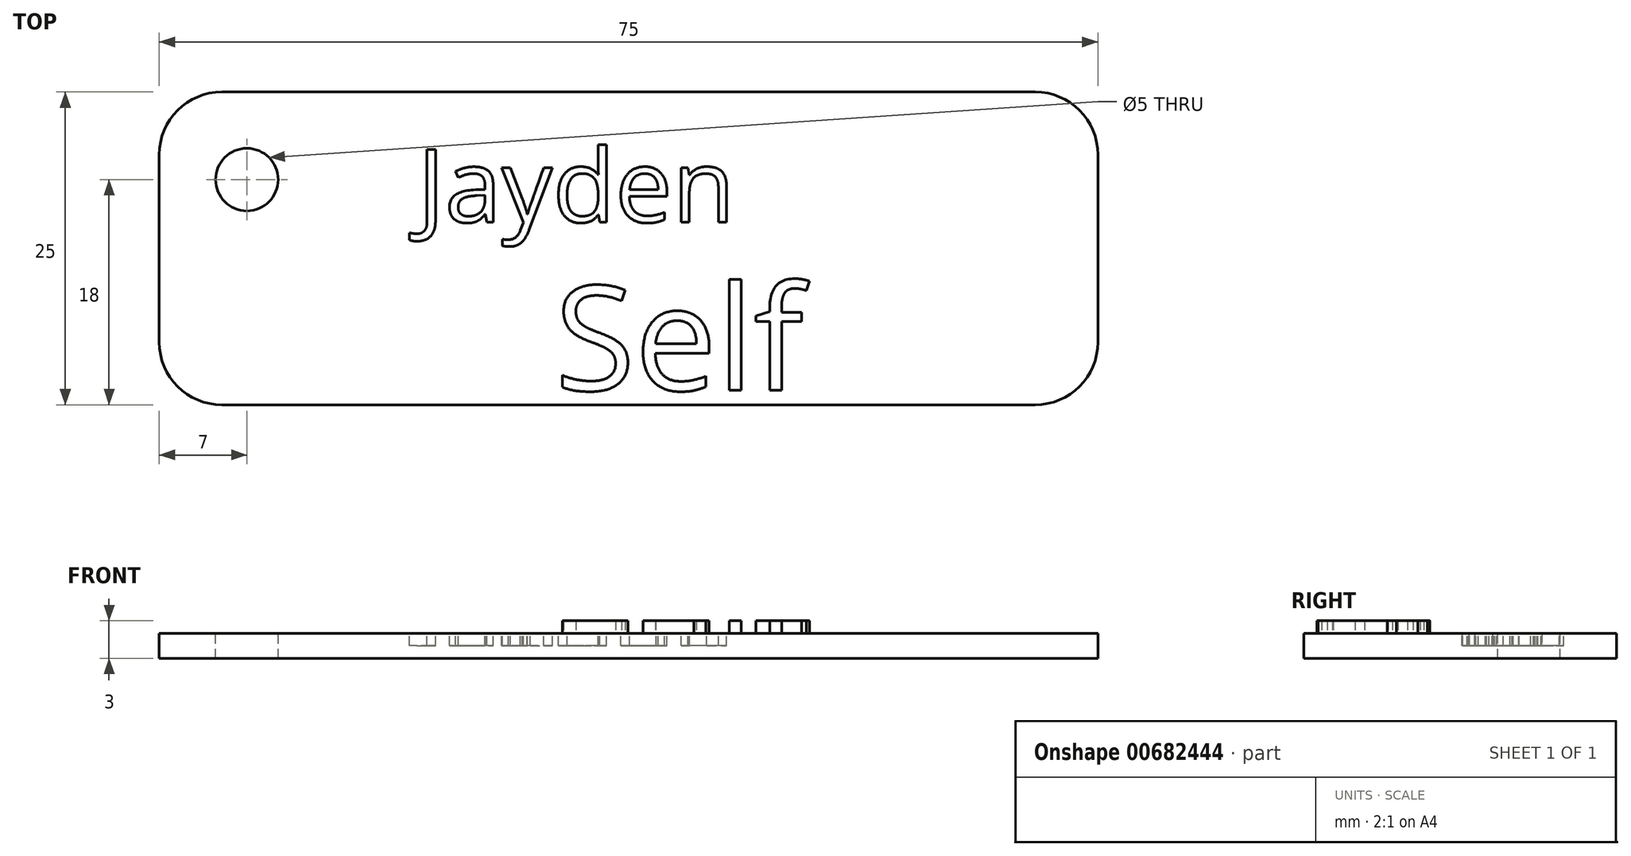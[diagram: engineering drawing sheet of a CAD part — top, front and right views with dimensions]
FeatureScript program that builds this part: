
annotation { "Feature Type Name" : "Feature", "Feature Type Description" : "" }
export const myFeature = defineFeature(function(context is Context, id is Id, definition is map)
    precondition{}
    {
        {
            var Q0;
            Q0=qCreatedBy(makeId("Top.planeOp"),FACE);
            var sketch = newSketch(context, id + "F0", { "sketchPlane" : qUnion([Q0])});
            skLineSegment(sketch, "E0.bottom", {"start": v(-32.5, 12.5) * mm, "end": v(32.5, 12.5) * mm});
            skLineSegment(sketch, "E0.top", {"start": v(-32.5, -12.5) * mm, "end": v(32.5, -12.5) * mm});
            skLineSegment(sketch, "E0.left", {"start": v(-37.5, 7.5) * mm, "end": v(-37.5, -7.5) * mm});
            skLineSegment(sketch, "E0.right", {"start": v(37.5, 7.5) * mm, "end": v(37.5, -7.5) * mm});
            skPoint(sketch, "E0.middle", {"position": v(0, 0) * mm});
            skPoint(sketch, "E1.visualSharp", {"position": v(-37.5, 12.5) * mm});
            skArc(sketch, "E1.filletArc", {"start": v(-32.5, 12.5) * mm, "mid": v(-36.04, 11.04) * mm, "end": v(-37.5, 7.5) * mm});
            skPoint(sketch, "E2.visualSharp", {"position": v(37.5, 12.5) * mm});
            skArc(sketch, "E2.filletArc", {"start": v(37.5, 7.5) * mm, "mid": v(36.04, 11.04) * mm, "end": v(32.5, 12.5) * mm});
            skPoint(sketch, "E3.visualSharp", {"position": v(37.5, -12.5) * mm});
            skArc(sketch, "E3.filletArc", {"start": v(32.5, -12.5) * mm, "mid": v(36.04, -11.04) * mm, "end": v(37.5, -7.5) * mm});
            skPoint(sketch, "E4.visualSharp", {"position": v(-37.5, -12.5) * mm});
            skArc(sketch, "E4.filletArc", {"start": v(-37.5, -7.5) * mm, "mid": v(-36.04, -11.04) * mm, "end": v(-32.5, -12.5) * mm});
            skSolve(sketch);
        }
        {
            var Q0;
            Q0=makeQuery(id+"F0.imprint","IMPRINT",FACE,{"disambiguationData":[TD([[makeQuery(id+"F0.imprint","IMPRINT",EDGE,{"derivedFrom":sQuery(id+"F0.wireOp",EDGE,"E0.bottom")}),-1.0]])]});
            extrude(context, id + "F1", {"entities" : qUnion([Q0]), "depth" : 2 * mm, "offsetDistance" : 25.4 * mm});
        }
        {
            var Q0;
            Q0=makeQuery(id+"F1.opExtrude","CAP_FACE",FACE,{"disambiguationData":[OSD([sQuery(id+"F0.wireOp",EDGE,"E0.bottom"),sQuery(id+"F0.wireOp",EDGE,"E0.top"),sQuery(id+"F0.wireOp",EDGE,"E0.left"),sQuery(id+"F0.wireOp",EDGE,"E0.right"),sQuery(id+"F0.wireOp",EDGE,"E1.filletArc"),sQuery(id+"F0.wireOp",EDGE,"E2.filletArc"),sQuery(id+"F0.wireOp",EDGE,"E3.filletArc"),sQuery(id+"F0.wireOp",EDGE,"E4.filletArc")])],"isStart":false});
            var sketch = newSketch(context, id + "F2", { "sketchPlane" : qUnion([Q0])});
            skPoint(sketch, "E5", {"position": v(-30.5, 5.5) * mm});
            skSolve(sketch);
        }
        {
            var Q0;
            Q0=sQuery(id+"F2.wireOp",VERTEX,"E5");
            var Q1;
            Q1=makeQuery(id+"F1.opExtrude","SWEPT_BODY",BODY,{"disambiguationData":[OSD([sQuery(id+"F0.wireOp",EDGE,"E0.bottom"),sQuery(id+"F0.wireOp",EDGE,"E0.top"),sQuery(id+"F0.wireOp",EDGE,"E0.left"),sQuery(id+"F0.wireOp",EDGE,"E0.right"),sQuery(id+"F0.wireOp",EDGE,"E1.filletArc"),sQuery(id+"F0.wireOp",EDGE,"E2.filletArc"),sQuery(id+"F0.wireOp",EDGE,"E3.filletArc"),sQuery(id+"F0.wireOp",EDGE,"E4.filletArc")])]});
            hole(context, id + "F3", {"style" : HoleStyle.SIMPLE, "endStyle" : HoleEndStyle.THROUGH, "holeDiameter" : 5 * mm, "majorDiameter" : 5 * mm, "isTappedThrough" : true, "tappedDepth" : 12 * mm, "tapClearance" : 3, "locations" : qUnion([Q0]), "scope" : qUnion([Q1])});
        }
        {
            var Q0;
            Q0=makeQuery(id+"F1.opExtrude","CAP_FACE",FACE,{"disambiguationData":[OSD([sQuery(id+"F0.wireOp",EDGE,"E0.bottom"),sQuery(id+"F0.wireOp",EDGE,"E0.top"),sQuery(id+"F0.wireOp",EDGE,"E0.left"),sQuery(id+"F0.wireOp",EDGE,"E0.right"),sQuery(id+"F0.wireOp",EDGE,"E1.filletArc"),sQuery(id+"F0.wireOp",EDGE,"E2.filletArc"),sQuery(id+"F0.wireOp",EDGE,"E3.filletArc"),sQuery(id+"F0.wireOp",EDGE,"E4.filletArc")])],"isStart":false});
            var sketch = newSketch(context, id + "F4", { "sketchPlane" : qUnion([Q0])});
            skText(sketch, "E6", { "text": "Jayden", "fontName": "OpenSans-Regular.ttf"});
            const initialGuessF4  = {"E6": [-0.01686, 0.0021, 1, 0, 0.00586]};
            skSetInitialGuess(sketch, initialGuessF4);
            skSolve(sketch);
        }
        {
            var Q0;
            Q0 = qSketchRegion(id + "F4", true);
            extrude(context, id + "F5", {"entities" : qUnion([Q0]), "operationType" : NewBodyOperationType.REMOVE, "oppositeDirection" : true, "depth" : 1 * mm, "offsetDistance" : 25 * mm});
        }
        {
            var Q0;
            {var subQ0=sQuery(id+"F0.wireOp",EDGE,"E0.left");var subQ1=sQuery(id+"F0.wireOp",EDGE,"E0.top");var subQ2=sQuery(id+"F0.wireOp",EDGE,"E0.bottom");var subQ3=sQuery(id+"F0.wireOp",EDGE,"E0.right");var subQ4=sQuery(id+"F0.wireOp",EDGE,"E1.filletArc");var subQ5=sQuery(id+"F0.wireOp",EDGE,"E2.filletArc");var subQ6=sQuery(id+"F0.wireOp",EDGE,"E3.filletArc");var subQ7=sQuery(id+"F0.wireOp",EDGE,"E4.filletArc");Q0=makeQuery(id+"F5.boolean.opBoolean","SPLIT",FACE,{"disambiguationData":[TD([makeQuery(id+"F1.opExtrude","SWEPT_FACE",FACE,{"disambiguationData":[OSD([subQ2])]})])],"derivedFrom":makeQuery(id+"F1.opExtrude","CAP_FACE",FACE,{"disambiguationData":[OSD([subQ2,subQ1,subQ0,subQ3,subQ4,subQ5,subQ6,subQ7])],"isStart":false})});}
            var sketch = newSketch(context, id + "F6", { "sketchPlane" : qUnion([Q0])});
            skText(sketch, "E7", { "text": "Self", "fontName": "OpenSans-Regular.ttf"});
            const initialGuessF6  = {"E7": [-0.0059, -0.01134, 1, 0, 0.0084]};
            skSetInitialGuess(sketch, initialGuessF6);
            skSolve(sketch);
        }
        {
            var Q0;
            Q0 = qSketchRegion(id + "F6", true);
            var Q1;
            Q1 = qConstructionFilter(qBodyType(qCreatedBy(id + "F6" ,EDGE), BodyType.WIRE), ConstructionObject.NO);
            extrude(context, id + "F7", {"entities" : qUnion([Q0]), "operationType" : NewBodyOperationType.ADD, "surfaceEntities" : qUnion([Q1]), "depth" : 1 * mm, "offsetDistance" : 25 * mm});
        }
    });
